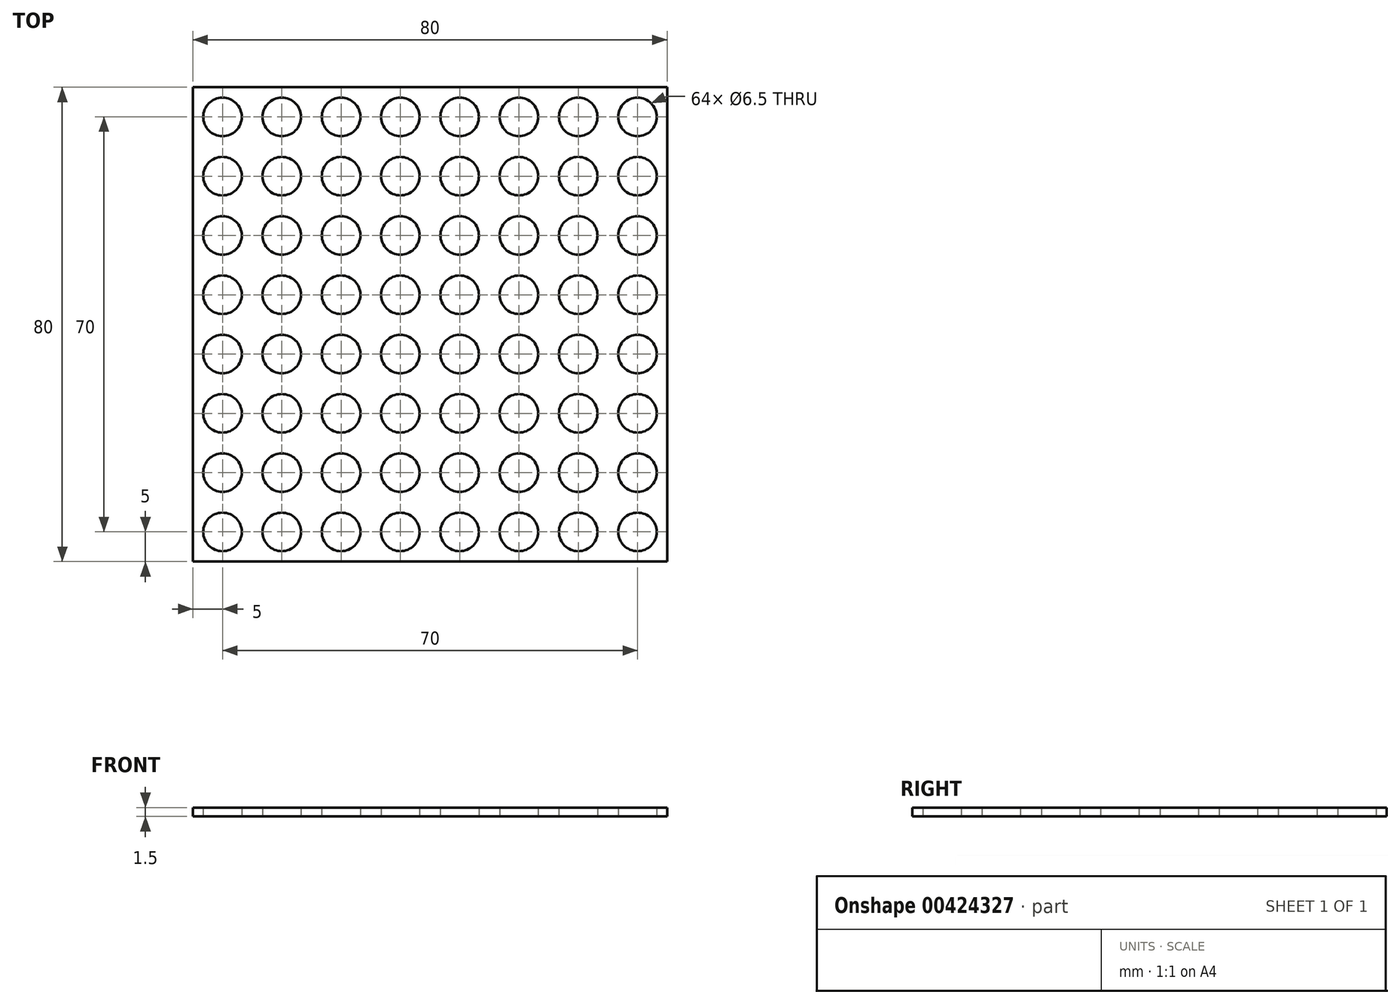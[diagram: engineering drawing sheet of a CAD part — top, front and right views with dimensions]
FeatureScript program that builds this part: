
annotation { "Feature Type Name" : "Feature", "Feature Type Description" : "" }
export const myFeature = defineFeature(function(context is Context, id is Id, definition is map)
    precondition{}
    {
        {
            var Q0;
            Q0=qCreatedBy(makeId("Top.planeOp"),FACE);
            var sketch = newSketch(context, id + "F0", { "sketchPlane" : qUnion([Q0])});
            skPoint(sketch, "E0.middle", {"position": v(0, 0) * mm});
            skCircle(sketch, "E1", {"center": v(-35, 35) * mm, "radius": 3.25 * mm});
            skLineSegment(sketch, "E2.bottom", {"start": v(-40, 40) * mm, "end": v(40, 40) * mm});
            skLineSegment(sketch, "E2.top", {"start": v(-40, -40) * mm, "end": v(40, -40) * mm});
            skLineSegment(sketch, "E2.left", {"start": v(-40, 40) * mm, "end": v(-40, -40) * mm});
            skLineSegment(sketch, "E2.right", {"start": v(40, 40) * mm, "end": v(40, -40) * mm});
            skCircle(sketch, "E3.0.1.0", {"center": v(-35, 25) * mm, "radius": 3.25 * mm});
            skCircle(sketch, "E3.0.2.0", {"center": v(-35, 15) * mm, "radius": 3.25 * mm});
            skCircle(sketch, "E3.0.3.0", {"center": v(-35, 5) * mm, "radius": 3.25 * mm});
            skCircle(sketch, "E3.0.4.0", {"center": v(-35, -5) * mm, "radius": 3.25 * mm});
            skCircle(sketch, "E3.0.5.0", {"center": v(-35, -15) * mm, "radius": 3.25 * mm});
            skCircle(sketch, "E3.0.6.0", {"center": v(-35, -25) * mm, "radius": 3.25 * mm});
            skCircle(sketch, "E3.0.7.0", {"center": v(-35, -35) * mm, "radius": 3.25 * mm});
            skCircle(sketch, "E3.1.0.0", {"center": v(-25, 35) * mm, "radius": 3.25 * mm});
            skCircle(sketch, "E3.1.1.0", {"center": v(-25, 25) * mm, "radius": 3.25 * mm});
            skCircle(sketch, "E3.1.2.0", {"center": v(-25, 15) * mm, "radius": 3.25 * mm});
            skCircle(sketch, "E3.1.3.0", {"center": v(-25, 5) * mm, "radius": 3.25 * mm});
            skCircle(sketch, "E3.1.4.0", {"center": v(-25, -5) * mm, "radius": 3.25 * mm});
            skCircle(sketch, "E3.1.5.0", {"center": v(-25, -15) * mm, "radius": 3.25 * mm});
            skCircle(sketch, "E3.1.6.0", {"center": v(-25, -25) * mm, "radius": 3.25 * mm});
            skCircle(sketch, "E3.1.7.0", {"center": v(-25, -35) * mm, "radius": 3.25 * mm});
            skCircle(sketch, "E3.2.0.0", {"center": v(-15, 35) * mm, "radius": 3.25 * mm});
            skCircle(sketch, "E3.2.1.0", {"center": v(-15, 25) * mm, "radius": 3.25 * mm});
            skCircle(sketch, "E3.2.2.0", {"center": v(-15, 15) * mm, "radius": 3.25 * mm});
            skCircle(sketch, "E3.2.3.0", {"center": v(-15, 5) * mm, "radius": 3.25 * mm});
            skCircle(sketch, "E3.2.4.0", {"center": v(-15, -5) * mm, "radius": 3.25 * mm});
            skCircle(sketch, "E3.2.5.0", {"center": v(-15, -15) * mm, "radius": 3.25 * mm});
            skCircle(sketch, "E3.2.6.0", {"center": v(-15, -25) * mm, "radius": 3.25 * mm});
            skCircle(sketch, "E3.2.7.0", {"center": v(-15, -35) * mm, "radius": 3.25 * mm});
            skCircle(sketch, "E3.3.0.0", {"center": v(-5, 35) * mm, "radius": 3.25 * mm});
            skCircle(sketch, "E3.3.1.0", {"center": v(-5, 25) * mm, "radius": 3.25 * mm});
            skCircle(sketch, "E3.3.2.0", {"center": v(-5, 15) * mm, "radius": 3.25 * mm});
            skCircle(sketch, "E3.3.3.0", {"center": v(-5, 5) * mm, "radius": 3.25 * mm});
            skCircle(sketch, "E3.3.4.0", {"center": v(-5, -5) * mm, "radius": 3.25 * mm});
            skCircle(sketch, "E3.3.5.0", {"center": v(-5, -15) * mm, "radius": 3.25 * mm});
            skCircle(sketch, "E3.3.6.0", {"center": v(-5, -25) * mm, "radius": 3.25 * mm});
            skCircle(sketch, "E3.3.7.0", {"center": v(-5, -35) * mm, "radius": 3.25 * mm});
            skCircle(sketch, "E3.4.0.0", {"center": v(5, 35) * mm, "radius": 3.25 * mm});
            skCircle(sketch, "E3.4.1.0", {"center": v(5, 25) * mm, "radius": 3.25 * mm});
            skCircle(sketch, "E3.4.2.0", {"center": v(5, 15) * mm, "radius": 3.25 * mm});
            skCircle(sketch, "E3.4.3.0", {"center": v(5, 5) * mm, "radius": 3.25 * mm});
            skCircle(sketch, "E3.4.4.0", {"center": v(5, -5) * mm, "radius": 3.25 * mm});
            skCircle(sketch, "E3.4.5.0", {"center": v(5, -15) * mm, "radius": 3.25 * mm});
            skCircle(sketch, "E3.4.6.0", {"center": v(5, -25) * mm, "radius": 3.25 * mm});
            skCircle(sketch, "E3.4.7.0", {"center": v(5, -35) * mm, "radius": 3.25 * mm});
            skCircle(sketch, "E3.5.0.0", {"center": v(15, 35) * mm, "radius": 3.25 * mm});
            skCircle(sketch, "E3.5.1.0", {"center": v(15, 25) * mm, "radius": 3.25 * mm});
            skCircle(sketch, "E3.5.2.0", {"center": v(15, 15) * mm, "radius": 3.25 * mm});
            skCircle(sketch, "E3.5.3.0", {"center": v(15, 5) * mm, "radius": 3.25 * mm});
            skCircle(sketch, "E3.5.4.0", {"center": v(15, -5) * mm, "radius": 3.25 * mm});
            skCircle(sketch, "E3.5.5.0", {"center": v(15, -15) * mm, "radius": 3.25 * mm});
            skCircle(sketch, "E3.5.6.0", {"center": v(15, -25) * mm, "radius": 3.25 * mm});
            skCircle(sketch, "E3.5.7.0", {"center": v(15, -35) * mm, "radius": 3.25 * mm});
            skCircle(sketch, "E3.6.0.0", {"center": v(25, 35) * mm, "radius": 3.25 * mm});
            skCircle(sketch, "E3.6.1.0", {"center": v(25, 25) * mm, "radius": 3.25 * mm});
            skCircle(sketch, "E3.6.2.0", {"center": v(25, 15) * mm, "radius": 3.25 * mm});
            skCircle(sketch, "E3.6.3.0", {"center": v(25, 5) * mm, "radius": 3.25 * mm});
            skCircle(sketch, "E3.6.4.0", {"center": v(25, -5) * mm, "radius": 3.25 * mm});
            skCircle(sketch, "E3.6.5.0", {"center": v(25, -15) * mm, "radius": 3.25 * mm});
            skCircle(sketch, "E3.6.6.0", {"center": v(25, -25) * mm, "radius": 3.25 * mm});
            skCircle(sketch, "E3.6.7.0", {"center": v(25, -35) * mm, "radius": 3.25 * mm});
            skCircle(sketch, "E3.7.0.0", {"center": v(35, 35) * mm, "radius": 3.25 * mm});
            skCircle(sketch, "E3.7.1.0", {"center": v(35, 25) * mm, "radius": 3.25 * mm});
            skCircle(sketch, "E3.7.2.0", {"center": v(35, 15) * mm, "radius": 3.25 * mm});
            skCircle(sketch, "E3.7.3.0", {"center": v(35, 5) * mm, "radius": 3.25 * mm});
            skCircle(sketch, "E3.7.4.0", {"center": v(35, -5) * mm, "radius": 3.25 * mm});
            skCircle(sketch, "E3.7.5.0", {"center": v(35, -15) * mm, "radius": 3.25 * mm});
            skCircle(sketch, "E3.7.6.0", {"center": v(35, -25) * mm, "radius": 3.25 * mm});
            skCircle(sketch, "E3.7.7.0", {"center": v(35, -35) * mm, "radius": 3.25 * mm});
            skLineSegment(sketch, "E3.direction1", {"start": v(-35, 35) * mm, "end": v(-25, 35) * mm, "construction": true});
            skLineSegment(sketch, "E3.direction2", {"start": v(-35, 35) * mm, "end": v(-35, 25) * mm, "construction": true});
            skSolve(sketch);
        }
        {
            var Q0;
            Q0=makeQuery(id+"F0.imprint","IMPRINT",FACE,{"disambiguationData":[TD([[makeQuery(id+"F0.imprint","IMPRINT",EDGE,{"derivedFrom":sQuery(id+"F0.wireOp",EDGE,"E1")}),-1.0]])]});
            extrude(context, id + "F1", {"entities" : qUnion([Q0]), "depth" : 1.5 * mm});
        }
    });
